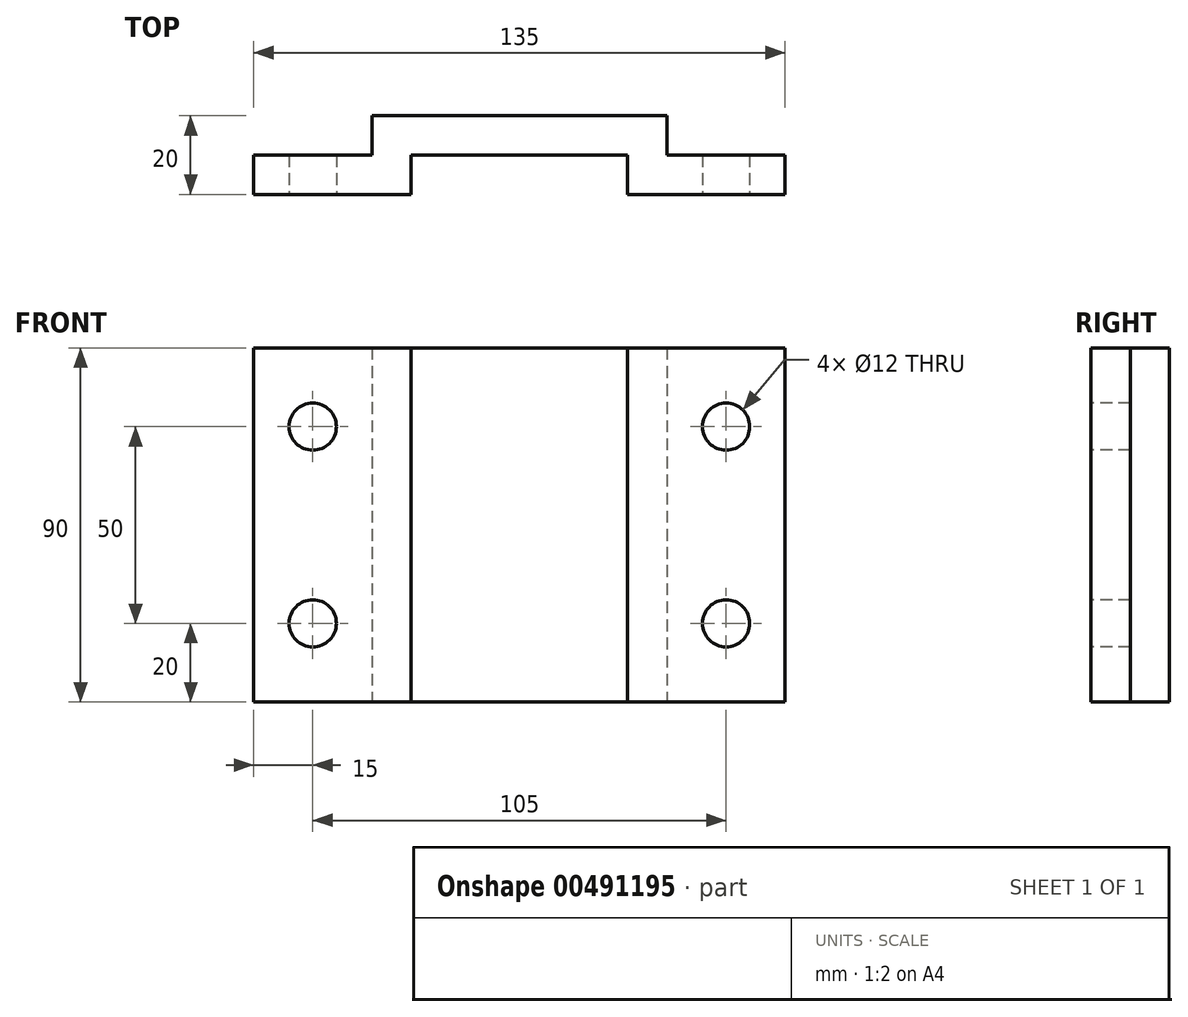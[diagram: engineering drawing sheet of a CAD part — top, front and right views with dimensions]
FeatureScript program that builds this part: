
annotation { "Feature Type Name" : "Feature", "Feature Type Description" : "" }
export const myFeature = defineFeature(function(context is Context, id is Id, definition is map)
    precondition{}
    {
        {
            var Q0;
            Q0=qCreatedBy(makeId("Top.planeOp"),FACE);
            var sketch = newSketch(context, id + "F0", { "sketchPlane" : qUnion([Q0])});
            skLineSegment(sketch, "E0", {"start": v(-70, 0) * mm, "end": v(-70, 10) * mm});
            skLineSegment(sketch, "E1", {"start": v(-70, 10) * mm, "end": v(-40, 10) * mm});
            skLineSegment(sketch, "E2", {"start": v(-40, 10) * mm, "end": v(-40, 20) * mm});
            skLineSegment(sketch, "E3", {"start": v(-40, 20) * mm, "end": v(35, 20) * mm});
            skLineSegment(sketch, "E4", {"start": v(35, 20) * mm, "end": v(35, 10) * mm});
            skLineSegment(sketch, "E5", {"start": v(35, 10) * mm, "end": v(65, 10) * mm});
            skLineSegment(sketch, "E6", {"start": v(65, 10) * mm, "end": v(65, 0) * mm});
            skLineSegment(sketch, "E7", {"start": v(65, 0) * mm, "end": v(25, 0) * mm});
            skLineSegment(sketch, "E8", {"start": v(25, 0) * mm, "end": v(25, 10) * mm});
            skLineSegment(sketch, "E9", {"start": v(25, 10) * mm, "end": v(-30, 10) * mm});
            skLineSegment(sketch, "E10", {"start": v(-30, 10) * mm, "end": v(-30, 0) * mm});
            skLineSegment(sketch, "E11", {"start": v(-30, 0) * mm, "end": v(-70, 0) * mm});
            skSolve(sketch);
        }
        {
            var Q0;
            Q0=makeQuery(id+"F0.imprint","IMPRINT",FACE,{"disambiguationData":[TD([[makeQuery(id+"F0.imprint","IMPRINT",EDGE,{"derivedFrom":sQuery(id+"F0.wireOp",EDGE,"E0")}),-1.0]])]});
            extrude(context, id + "F1", {"entities" : qUnion([Q0]), "depth" : 90 * mm});
        }
        {
            var Q0;
            Q0=qCreatedBy(makeId("Front.planeOp"),FACE);
            var sketch = newSketch(context, id + "F2", { "sketchPlane" : qUnion([Q0])});
            skCircle(sketch, "E12", {"center": v(-55, 20) * mm, "radius": 6 * mm});
            skCircle(sketch, "E13", {"center": v(-55, 70) * mm, "radius": 6 * mm});
            skLineSegment(sketch, "E14", {"start": v(-2.5, 103.78) * mm, "end": v(-2.5, -19.66) * mm, "construction": true});
            skCircle(sketch, "E15.MirrorC", {"center": v(50, 70) * mm, "radius": 6 * mm});
            skCircle(sketch, "E16.MirrorC", {"center": v(50, 20) * mm, "radius": 6 * mm});
            skSolve(sketch);
        }
        {
            var Q0;
            Q0 = qSketchRegion(id + "F2", true);
            extrude(context, id + "F3", {"entities" : qUnion([Q0]), "operationType" : NewBodyOperationType.REMOVE, "endBound" : BoundingType.THROUGH_ALL, "oppositeDirection" : true, "depth" : 25 * mm});
        }
    });
